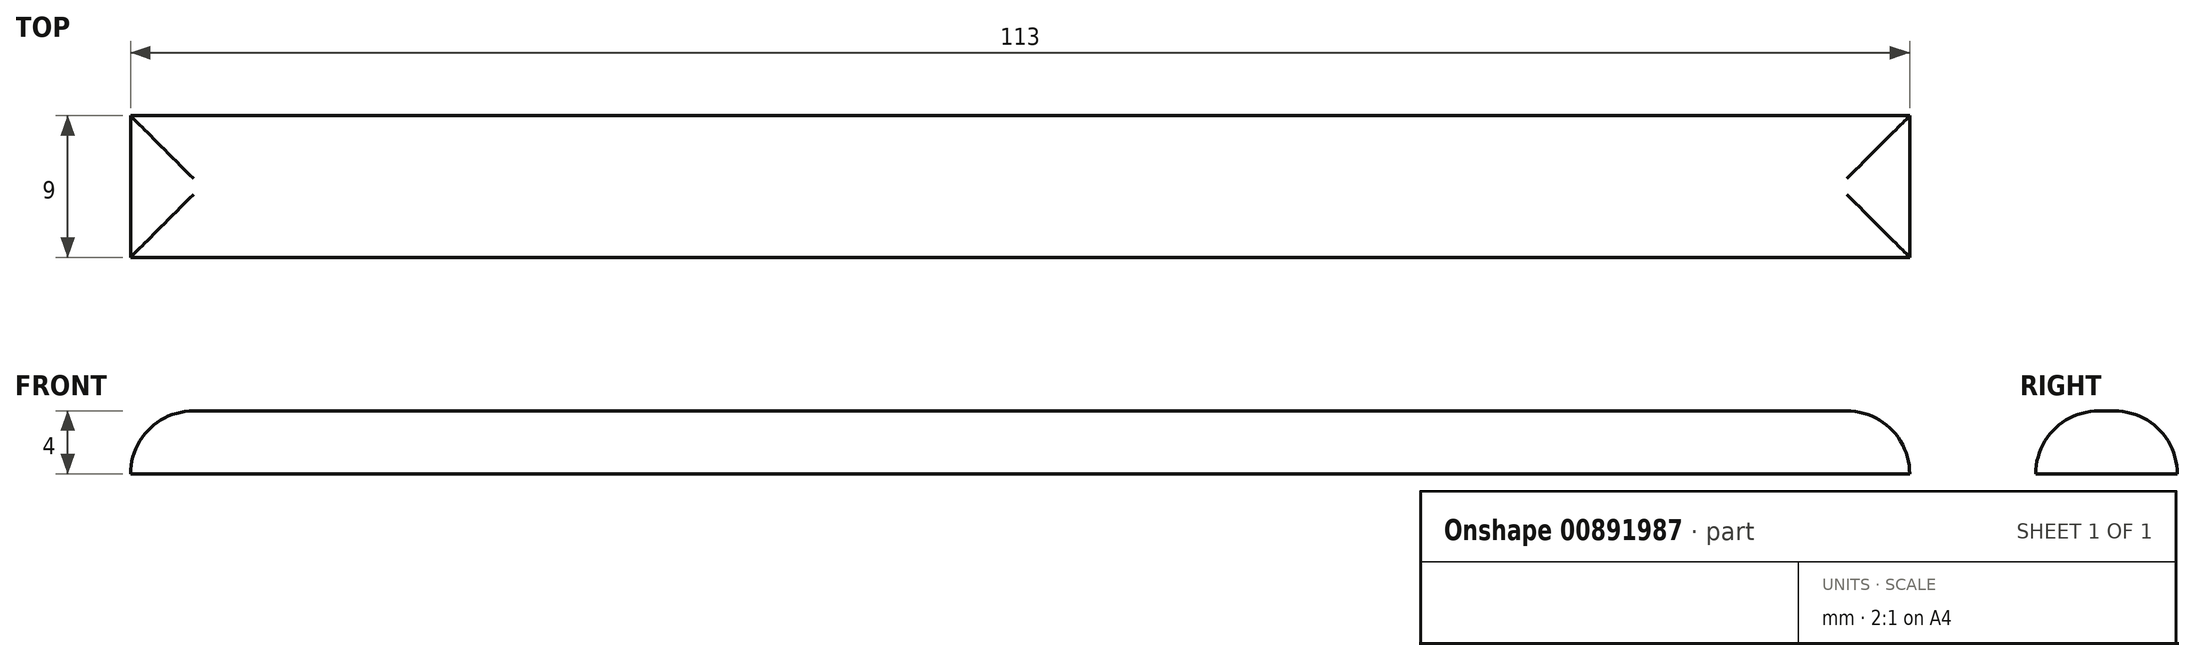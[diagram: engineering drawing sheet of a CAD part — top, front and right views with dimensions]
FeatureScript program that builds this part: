
annotation { "Feature Type Name" : "Feature", "Feature Type Description" : "" }
export const myFeature = defineFeature(function(context is Context, id is Id, definition is map)
    precondition{}
    {
        {
            var Q0;
            Q0=qCreatedBy(makeId("Top.planeOp"),FACE);
            var sketch = newSketch(context, id + "F0", { "sketchPlane" : qUnion([Q0])});
            skLineSegment(sketch, "E0.bottom", {"start": v(56.5, -4.5) * mm, "end": v(-56.5, -4.5) * mm});
            skLineSegment(sketch, "E0.top", {"start": v(56.5, 4.5) * mm, "end": v(-56.5, 4.5) * mm});
            skLineSegment(sketch, "E0.left", {"start": v(56.5, -4.5) * mm, "end": v(56.5, 4.5) * mm});
            skLineSegment(sketch, "E0.right", {"start": v(-56.5, -4.5) * mm, "end": v(-56.5, 4.5) * mm});
            skPoint(sketch, "E0.middle", {"position": v(0, 0) * mm});
            skSolve(sketch);
        }
        {
            var Q0;
            Q0=makeQuery(id+"F0.imprint","IMPRINT",FACE,{"disambiguationData":[TD([[makeQuery(id+"F0.imprint","IMPRINT",EDGE,{"derivedFrom":sQuery(id+"F0.wireOp",EDGE,"E0.bottom")}),-1.0]])]});
            extrude(context, id + "F1", {"entities" : qUnion([Q0]), "depth" : 4 * mm, "offsetDistance" : 25 * mm});
        }
        {
            var Q0;
            Q0=makeQuery(id+"F1.opExtrude","CAP_EDGE",EDGE,{"disambiguationData":[OSD([sQuery(id+"F0.wireOp",EDGE,"E0.top")])],"isStart":false});
            var Q1;
            Q1=makeQuery(id+"F1.opExtrude","CAP_EDGE",EDGE,{"disambiguationData":[OSD([sQuery(id+"F0.wireOp",EDGE,"E0.bottom")])],"isStart":false});
            var Q2;
            Q2=makeQuery(id+"F1.opExtrude","CAP_EDGE",EDGE,{"disambiguationData":[OSD([sQuery(id+"F0.wireOp",EDGE,"E0.right")])],"isStart":false});
            var Q3;
            Q3=makeQuery(id+"F1.opExtrude","CAP_EDGE",EDGE,{"disambiguationData":[OSD([sQuery(id+"F0.wireOp",EDGE,"E0.left")])],"isStart":false});
            fillet(context, id + "F2", {"entities" : qUnion([Q0, Q1, Q2, Q3]), "radius" : 4 * mm, "tangentPropagation" : true, "allowEdgeOverflow" : false});
        }
    });
